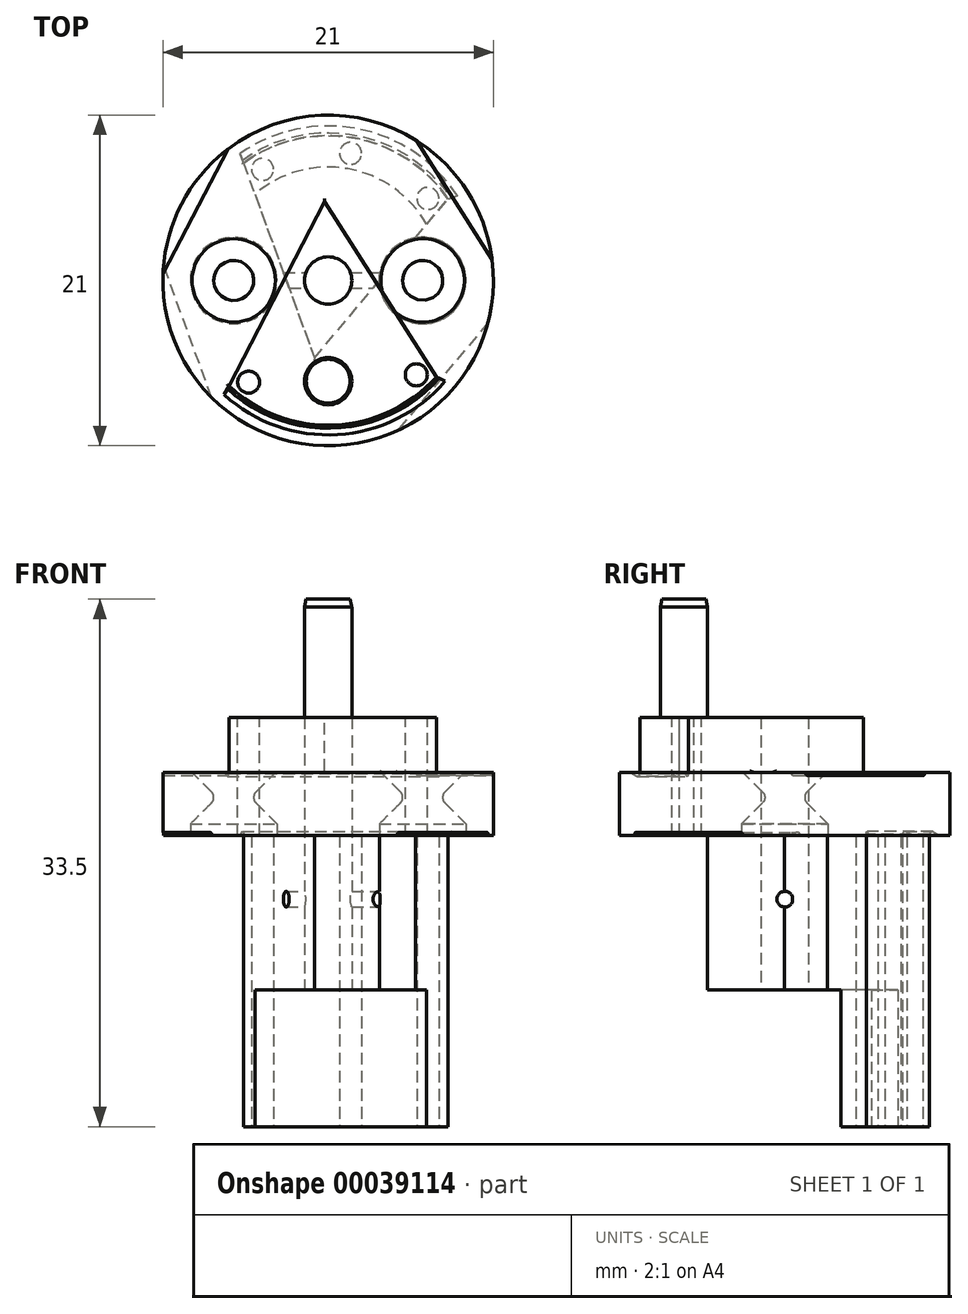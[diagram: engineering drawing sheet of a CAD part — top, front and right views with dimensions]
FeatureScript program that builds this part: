
annotation { "Feature Type Name" : "Feature", "Feature Type Description" : "" }
export const myFeature = defineFeature(function(context is Context, id is Id, definition is map)
    precondition{}
    {
        {
            var Q0;
            Q0=qCreatedBy(makeId("Front.planeOp"),FACE);
            var sketch = newSketch(context, id + "F0", { "sketchPlane" : qUnion([Q0])});
            skLineSegment(sketch, "E0.bottom", {"start": v(-9.2, 26) * mm, "end": v(0, 26) * mm});
            skLineSegment(sketch, "E0.top", {"start": v(-9.2, 0) * mm, "end": v(0, 0) * mm});
            skLineSegment(sketch, "E0.left", {"start": v(-9.2, 18.5) * mm, "end": v(-9.2, 0) * mm});
            skLineSegment(sketch, "E1.bottom", {"start": v(-9.2, 26) * mm, "end": v(-10.5, 26) * mm});
            skLineSegment(sketch, "E1.top", {"start": v(-9.2, 18.5) * mm, "end": v(-10.5, 18.5) * mm});
            skLineSegment(sketch, "E1.right", {"start": v(-10.5, 26) * mm, "end": v(-10.5, 18.5) * mm});
            skLineSegment(sketch, "E2", {"start": v(0, 0) * mm, "end": v(0, 26) * mm});
            skPoint(sketch, "E0.right.start.orphan", {"position": v(9.2, 26) * mm});
            skSolve(sketch);
        }
        {
            var Q0;
            Q0=makeQuery(id+"F0.imprint","IMPRINT",FACE,{"disambiguationData":[TD([[makeQuery(id+"F0.imprint","IMPRINT",EDGE,{"derivedFrom":sQuery(id+"F0.wireOp",EDGE,"E0.bottom")}),-1.0]])]});
            var Q1;
            Q1=sQuery(id+"F0.wireOp",EDGE,"E2");
            revolve(context, id + "F1", {"entities" : qUnion([Q0]), "axis" : qUnion([Q1]), "revolveType" : RevolveType.FULL});
        }
        {
            var Q0;
            Q0=makeQuery(id+"F1.opRevolve","SWEPT_FACE",FACE,{"disambiguationData":[OSD([sQuery(id+"F0.wireOp",EDGE,"E0.top")])]});
            var sketch = newSketch(context, id + "F2", { "sketchPlane" : qUnion([Q0])});
            skCircle(sketch, "E3", {"center": v(0, 0) * mm, "radius": 7.2 * mm});
            skSolve(sketch);
        }
        {
            var Q0;
            Q0=makeQuery(id+"F2.imprint","IMPRINT",FACE,{"disambiguationData":[TD([[makeQuery(id+"F2.imprint","IMPRINT",EDGE,{"derivedFrom":sQuery(id+"F2.wireOp",EDGE,"E3")}),1.0]])]});
            extrude(context, id + "F3", {"entities" : qUnion([Q0]), "operationType" : NewBodyOperationType.REMOVE, "oppositeDirection" : true, "depth" : 8.7 * mm});
        }
        {
            var Q0;
            Q0=makeQuery(id+"F3.boolean.opBoolean","COPY",FACE,{"derivedFrom":makeQuery(id+"F3.opExtrude","CAP_FACE",FACE,{"disambiguationData":[OSD([sQuery(id+"F2.wireOp",EDGE,"E3")])],"isStart":false})});
            var sketch = newSketch(context, id + "F4", { "sketchPlane" : qUnion([Q0])});
            skPoint(sketch, "E4", {"position": v(-5.84, -8.73) * mm});
            skLineSegment(sketch, "E5", {"start": v(-5.84, -8.73) * mm, "end": v(-0.87, 4.92) * mm});
            skLineSegment(sketch, "E6", {"start": v(-0.87, 4.92) * mm, "end": v(8.47, -6.2) * mm});
            skPoint(sketch, "E7", {"position": v(0, 3.89) * mm});
            skCircle(sketch, "E8", {"center": v(0, 0) * mm, "radius": 2.5 * mm, "construction": true});
            skCircle(sketch, "E9", {"center": v(0, 0) * mm, "radius": 1.5 * mm});
            skArc(sketch, "E10", {"start": v(8.47, -6.2) * mm, "mid": v(-1.82, 10.34) * mm, "end": v(-5.84, -8.73) * mm});
            skCircle(sketch, "E11", {"center": v(1.42, -8.08) * mm, "radius": 0.7 * mm});
            skCircle(sketch, "E12", {"center": v(6.33, -5.21) * mm, "radius": 0.7 * mm});
            skCircle(sketch, "E13", {"center": v(-4.17, -7.06) * mm, "radius": 0.7 * mm});
            skLineSegment(sketch, "E14", {"start": v(1.42, -8.08) * mm, "end": v(0, 0) * mm, "construction": true});
            skLineSegment(sketch, "E15", {"start": v(10.15, 2.68) * mm, "end": v(4.4, 9.53) * mm});
            skLineSegment(sketch, "E16", {"start": v(-7.4, 7.45) * mm, "end": v(-10.46, -0.95) * mm});
            skSolve(sketch);
        }
        {
            var Q0;
            Q0 = qSketchRegion(id + "F4", true);
            var Q1;
            Q1=makeQuery(id+"F1.opRevolve","SWEPT_FACE",FACE,{"disambiguationData":[OSD([sQuery(id+"F0.wireOp",EDGE,"E0.top")])]});
            extrude(context, id + "F5", {"entities" : qUnion([Q0]), "operationType" : NewBodyOperationType.REMOVE, "oppositeDirection" : true, "depth" : 9.8 * mm, "hasSecondDirection" : true, "secondDirectionBound" : SecondDirectionBoundingType.UP_TO_SURFACE, "secondDirectionOppositeDirection" : false, "secondDirectionBoundEntityFace" : qUnion([Q1]), "secondDirectionDepth" : 25 * mm});
        }
        {
            var Q0;
            {var subQ0=sQuery(id+"F4.wireOp",EDGE,"E15");Q0=makeQuery(id+"F4.imprint","IMPRINT",FACE,{"disambiguationData":[TD([[makeQuery(id+"F4.imprint","IMPRINT",EDGE,{"derivedFrom":subQ0}),-1.0]])]});}
            var Q1;
            {var subQ0=sQuery(id+"F4.wireOp",EDGE,"E16");Q1=makeQuery(id+"F4.imprint","IMPRINT",FACE,{"disambiguationData":[TD([[makeQuery(id+"F4.imprint","IMPRINT",EDGE,{"derivedFrom":subQ0}),-1.0]])]});}
            extrude(context, id + "F6", {"entities" : qUnion([Q0, Q1]), "operationType" : NewBodyOperationType.REMOVE, "oppositeDirection" : true, "depth" : 10 * mm});
        }
        {
            var Q0;
            Q0=makeQuery(id+"F1.opRevolve","SWEPT_FACE",FACE,{"disambiguationData":[OSD([sQuery(id+"F0.wireOp",EDGE,"E0.bottom"),sQuery(id+"F0.wireOp",EDGE,"E1.bottom")])]});
            var sketch = newSketch(context, id + "F7", { "sketchPlane" : qUnion([Q0])});
            skCircle(sketch, "E17", {"center": v(0, 0) * mm, "radius": 2.5 * mm, "construction": true});
            skLineSegment(sketch, "E18", {"start": v(7.59, -7.26) * mm, "end": v(-0.22, 5) * mm});
            skLineSegment(sketch, "E19", {"start": v(-0.22, 5) * mm, "end": v(-6.93, -7.9) * mm});
            skArc(sketch, "E20", {"start": v(7.59, -7.26) * mm, "mid": v(-0.46, 10.5) * mm, "end": v(-6.93, -7.9) * mm});
            skLineSegment(sketch, "E21", {"start": v(10.42, 1.33) * mm, "end": v(5.6, 8.88) * mm});
            skLineSegment(sketch, "E22", {"start": v(-10.5, 0.42) * mm, "end": v(-6.36, 8.35) * mm});
            skArc(sketch, "E23", {"start": v(-6.3, -6.7) * mm, "mid": v(0.4, -9.2) * mm, "end": v(6.87, -6.12) * mm});
            skArc(sketch, "E24", {"start": v(-6.93, -7.9) * mm, "mid": v(0.46, -10.5) * mm, "end": v(7.59, -7.26) * mm});
            skSolve(sketch);
        }
        {
            var Q0;
            {var subQ0=sQuery(id+"F7.wireOp",EDGE,"E21");Q0=makeQuery(id+"F7.imprint","IMPRINT",FACE,{"disambiguationData":[TD([[makeQuery(id+"F7.imprint","IMPRINT",EDGE,{"derivedFrom":subQ0}),-1.0]])]});}
            var Q1;
            {var subQ5=sQuery(id+"F7.wireOp",EDGE,"E18");Q1=makeQuery(id+"F7.imprint","IMPRINT",FACE,{"disambiguationData":[TD([[makeQuery(id+"F7.imprint","IMPRINT",EDGE,{"derivedFrom":subQ5}),-1.0]])]});}
            var Q2;
            {var subQ0=sQuery(id+"F7.wireOp",EDGE,"E22");Q2=makeQuery(id+"F7.imprint","IMPRINT",FACE,{"disambiguationData":[TD([[makeQuery(id+"F7.imprint","IMPRINT",EDGE,{"derivedFrom":subQ0}),1.0]])]});}
            var Q3;
            Q3=makeQuery(id+"F7.imprint","IMPRINT",FACE,{"disambiguationData":[TD([[makeQuery(id+"F7.imprint","IMPRINT",EDGE,{"derivedFrom":sQuery(id+"F7.wireOp",EDGE,"75845bfa-6e58-4d6f-9768-84c6fc873f1d")}),1.0]])]});
            var Q4;
            Q4=makeQuery(id+"F7.imprint","IMPRINT",FACE,{"disambiguationData":[TD([[makeQuery(id+"F7.imprint","IMPRINT",EDGE,{"derivedFrom":sQuery(id+"F7.wireOp",EDGE,"bd788875-77d4-44b3-9050-4ba9302ed74b")}),1.0]])]});
            var Q5;
            {var subQ1=sQuery(id+"F7.wireOp",EDGE,"E23");Q5=makeQuery(id+"F7.imprint","IMPRINT",FACE,{"disambiguationData":[TD([[makeQuery(id+"F7.imprint","IMPRINT",EDGE,{"derivedFrom":subQ1}),-1.0]])]});}
            extrude(context, id + "F8", {"entities" : qUnion([Q0, Q1, Q2, Q3, Q4, Q5]), "operationType" : NewBodyOperationType.REMOVE, "oppositeDirection" : true, "depth" : 3.5 * mm});
        }
        {
            var Q0;
            Q0=makeQuery(id+"F1.opRevolve","SWEPT_FACE",FACE,{"disambiguationData":[OSD([sQuery(id+"F0.wireOp",EDGE,"E0.bottom"),sQuery(id+"F0.wireOp",EDGE,"E1.bottom")])]});
            var sketch = newSketch(context, id + "F9", { "sketchPlane" : qUnion([Q0])});
            skCircle(sketch, "E25", {"center": v(0, 0) * mm, "radius": 1.5 * mm});
            skCircle(sketch, "E26", {"center": v(0, -6.4) * mm, "radius": 1.5 * mm});
            skCircle(sketch, "E27", {"center": v(5.6, -6) * mm, "radius": 0.7 * mm});
            skCircle(sketch, "E28", {"center": v(-5.05, -6.46) * mm, "radius": 0.7 * mm});
            skSolve(sketch);
        }
        {
            var Q0;
            Q0=makeQuery(id+"F9.imprint","IMPRINT",FACE,{"disambiguationData":[TD([[makeQuery(id+"F9.imprint","IMPRINT",EDGE,{"derivedFrom":sQuery(id+"F9.wireOp",EDGE,"E25")}),1.0]])]});
            var Q1;
            Q1=makeQuery(id+"F9.imprint","IMPRINT",FACE,{"disambiguationData":[TD([[makeQuery(id+"F9.imprint","IMPRINT",EDGE,{"derivedFrom":sQuery(id+"F9.wireOp",EDGE,"E27")}),1.0]])]});
            var Q2;
            Q2=makeQuery(id+"F9.imprint","IMPRINT",FACE,{"disambiguationData":[TD([[makeQuery(id+"F9.imprint","IMPRINT",EDGE,{"derivedFrom":sQuery(id+"F9.wireOp",EDGE,"E28")}),1.0]])]});
            extrude(context, id + "F10", {"entities" : qUnion([Q0, Q1, Q2]), "operationType" : NewBodyOperationType.REMOVE, "endBound" : BoundingType.UP_TO_NEXT, "oppositeDirection" : true, "depth" : 25 * mm});
        }
        {
            var Q0;
            {var subQ0=sQuery(id+"F7.wireOp",EDGE,"E21");Q0=makeQuery(id+"F7.imprint","IMPRINT",FACE,{"disambiguationData":[TD([[makeQuery(id+"F7.imprint","IMPRINT",EDGE,{"derivedFrom":subQ0}),-1.0]])]});}
            var Q1;
            {var subQ0=sQuery(id+"F7.wireOp",EDGE,"E22");Q1=makeQuery(id+"F7.imprint","IMPRINT",FACE,{"disambiguationData":[TD([[makeQuery(id+"F7.imprint","IMPRINT",EDGE,{"derivedFrom":subQ0}),1.0]])]});}
            extrude(context, id + "F11", {"entities" : qUnion([Q0, Q1]), "operationType" : NewBodyOperationType.REMOVE, "oppositeDirection" : true, "depth" : 3.7 * mm});
        }
        {
            var Q0;
            Q0=makeQuery(id+"F9.imprint","IMPRINT",FACE,{"disambiguationData":[TD([[makeQuery(id+"F9.imprint","IMPRINT",EDGE,{"derivedFrom":sQuery(id+"F9.wireOp",EDGE,"E26")}),1.0]])]});
            extrude(context, id + "F12", {"entities" : qUnion([Q0]), "operationType" : NewBodyOperationType.ADD, "depth" : 7.5 * mm});
        }
        {
            var Q0;
            Q0=makeQuery(id+"F12.opExtrude","CAP_EDGE",EDGE,{"disambiguationData":[OSD([sQuery(id+"F9.wireOp",EDGE,"E26")])],"isStart":false});
            chamfer(context, id + "F13", {"entities" : qUnion([Q0]), "chamferType" : ChamferType.OFFSET_ANGLE, "width" : 0.5 * mm, "oppositeDirection" : true, "angle" : 12 * degree, "tangentPropagation" : true});
        }
        {
            var Q0;
            Q0=qCreatedBy(makeId("Front.planeOp"),FACE);
            var sketch = newSketch(context, id + "F14", { "sketchPlane" : qUnion([Q0])});
            skLineSegment(sketch, "E29", {"start": v(-6, 22.5) * mm, "end": v(-6, 19.26) * mm});
            skLineSegment(sketch, "E30", {"start": v(-6, 22.5) * mm, "end": v(-8.65, 22.5) * mm});
            skLineSegment(sketch, "E31", {"start": v(-8.65, 22.5) * mm, "end": v(-7.42, 21.27) * mm});
            skLineSegment(sketch, "E32", {"start": v(-8.75, 19.23) * mm, "end": v(-7.42, 20.56) * mm});
            skArc(sketch, "E33", {"start": v(-7.42, 20.56) * mm, "mid": v(-7.27, 20.91) * mm, "end": v(-7.42, 21.27) * mm});
            skCircle(sketch, "E34", {"center": v(-6, 18.5) * mm, "radius": 2.5 * mm, "construction": true});
            skLineSegment(sketch, "E35.top", {"start": v(-6, 18.5) * mm, "end": v(-8.75, 18.5) * mm});
            skLineSegment(sketch, "E35.left", {"start": v(-6, 19.26) * mm, "end": v(-6, 18.5) * mm});
            skLineSegment(sketch, "E35.right", {"start": v(-8.75, 19.23) * mm, "end": v(-8.75, 18.5) * mm});
            skSolve(sketch);
        }
        {
            var Q0;
            Q0 = qSketchRegion(id + "F14", true);
            var Q1;
            Q1=sQuery(id+"F14.wireOp",EDGE,"E29");
            revolve(context, id + "F15", {"operationType" : NewBodyOperationType.REMOVE, "entities" : qUnion([Q0]), "axis" : qUnion([Q1]), "revolveType" : RevolveType.FULL, "oppositeDirection" : true});
        }
        {
            var Q0;
            Q0=qCreatedBy(makeId("Front.planeOp"),FACE);
            var sketch = newSketch(context, id + "F16", { "sketchPlane" : qUnion([Q0])});
            skLineSegment(sketch, "E36", {"start": v(6, 22.5) * mm, "end": v(6, 21.29) * mm});
            skLineSegment(sketch, "E37", {"start": v(6, 22.5) * mm, "end": v(3.35, 22.5) * mm});
            skLineSegment(sketch, "E38", {"start": v(3.35, 22.5) * mm, "end": v(4.58, 21.27) * mm});
            skLineSegment(sketch, "E39", {"start": v(3.25, 19.23) * mm, "end": v(4.58, 20.56) * mm});
            skArc(sketch, "E40", {"start": v(4.58, 20.56) * mm, "mid": v(4.73, 20.91) * mm, "end": v(4.58, 21.27) * mm});
            skCircle(sketch, "E41", {"center": v(6, 18.5) * mm, "radius": 2.5 * mm, "construction": true});
            skLineSegment(sketch, "E42.top", {"start": v(6, 18.5) * mm, "end": v(3.25, 18.5) * mm});
            skLineSegment(sketch, "E42.left", {"start": v(6, 21.29) * mm, "end": v(6, 18.5) * mm});
            skLineSegment(sketch, "E42.right", {"start": v(3.25, 19.23) * mm, "end": v(3.25, 18.5) * mm});
            skLineSegment(sketch, "E43", {"start": v(3.25, 18.5) * mm, "end": v(3.25, 8.7) * mm});
            skLineSegment(sketch, "E44", {"start": v(3.25, 8.7) * mm, "end": v(6, 8.7) * mm});
            skLineSegment(sketch, "E45", {"start": v(6, 8.7) * mm, "end": v(6, 18.5) * mm});
            skSolve(sketch);
        }
        {
            var Q0;
            Q0=makeQuery(id+"F16.imprint","IMPRINT",FACE,{"disambiguationData":[TD([[makeQuery(id+"F16.imprint","IMPRINT",EDGE,{"derivedFrom":sQuery(id+"F16.wireOp",EDGE,"E36")}),-1.0]])]});
            var Q1;
            Q1=makeQuery(id+"F16.imprint","IMPRINT",FACE,{"disambiguationData":[TD([[makeQuery(id+"F16.imprint","IMPRINT",EDGE,{"derivedFrom":sQuery(id+"F16.wireOp",EDGE,"E42.top")}),1.0]])]});
            var Q2;
            Q2=sQuery(id+"F16.wireOp",EDGE,"E42.left");
            revolve(context, id + "F17", {"operationType" : NewBodyOperationType.REMOVE, "entities" : qUnion([Q0, Q1]), "axis" : qUnion([Q2]), "revolveType" : RevolveType.FULL, "oppositeDirection" : true});
        }
        {
            var Q0;
            Q0=makeQuery(id+"F8.boolean.opBoolean","COPY",FACE,{"derivedFrom":makeQuery(id+"F8.opExtrude","SWEPT_FACE",FACE,{"disambiguationData":[OSD([sQuery(id+"F7.wireOp",EDGE,"E19")])]})});
            var sketch = newSketch(context, id + "F18", { "sketchPlane" : qUnion([Q0])});
            skLineSegment(sketch, "E46", {"start": v(8.85, 22.5) * mm, "end": v(9.49, 22.5) * mm});
            skLineSegment(sketch, "E47", {"start": v(9.49, 22.5) * mm, "end": v(9.05, 22.25) * mm});
            skPoint(sketch, "E48", {"position": v(9.05, 22.45) * mm});
            skArc(sketch, "E49", {"start": v(9.05, 22.25) * mm, "mid": v(8.91, 22.3) * mm, "end": v(8.85, 22.45) * mm});
            skLineSegment(sketch, "E50", {"start": v(8.85, 22.5) * mm, "end": v(8.85, 22.45) * mm});
            skSolve(sketch);
        }
        {
            var Q0;
            Q0 = qSketchRegion(id + "F18", true);
            var Q1;
            Q1=makeQuery(id+"F8.boolean.opBoolean","COPY",EDGE,{"derivedFrom":makeQuery(id+"F8.opExtrude","CAP_EDGE",EDGE,{"disambiguationData":[OSD([sQuery(id+"F7.wireOp",EDGE,"E23")])],"isStart":false})});
            sweep(context, id + "F19", {"operationType" : NewBodyOperationType.REMOVE, "profiles" : qUnion([Q0]), "path" : qUnion([Q1])});
        }
        {
            var Q0;
            Q0=makeQuery(id+"F5.boolean.opBoolean","COPY",FACE,{"derivedFrom":makeQuery(id+"F5.opExtrude","SWEPT_FACE",FACE,{"disambiguationData":[OSD([sQuery(id+"F4.wireOp",EDGE,"E5")])]})});
            var sketch = newSketch(context, id + "F20", { "sketchPlane" : qUnion([Q0])});
            skLineSegment(sketch, "E51", {"start": v(-8.85, 18.5) * mm, "end": v(-9.49, 18.5) * mm});
            skLineSegment(sketch, "E52", {"start": v(-9.49, 18.5) * mm, "end": v(-9.05, 18.75) * mm});
            skPoint(sketch, "E53", {"position": v(-9.05, 18.55) * mm});
            skArc(sketch, "E54", {"start": v(-9.05, 18.75) * mm, "mid": v(-8.91, 18.7) * mm, "end": v(-8.85, 18.55) * mm});
            skLineSegment(sketch, "E55", {"start": v(-8.85, 18.55) * mm, "end": v(-8.85, 18.5) * mm});
            skSolve(sketch);
        }
        {
            var Q0;
            Q0=makeQuery(id+"F20.imprint","IMPRINT",FACE,{"disambiguationData":[TD([[makeQuery(id+"F20.imprint","IMPRINT",EDGE,{"derivedFrom":sQuery(id+"F20.wireOp",EDGE,"E51")}),-1.0]])]});
            var Q1;
            Q1=makeQuery(id+"F1.opRevolve","SWEPT_EDGE",EDGE,{"disambiguationData":[OSD([sQuery(id+"F0.wireOp",EDGE,"E0.left"),sQuery(id+"F0.wireOp",EDGE,"E1.top")])]});
            sweep(context, id + "F21", {"operationType" : NewBodyOperationType.REMOVE, "profiles" : qUnion([Q0]), "path" : qUnion([Q1])});
        }
        {
            var Q0;
            Q0=makeQuery(id+"F5.boolean.opBoolean","COPY",EDGE,{"derivedFrom":makeQuery(id+"F5.opExtrude","CAP_EDGE",EDGE,{"disambiguationData":[OSD([sQuery(id+"F4.wireOp",EDGE,"E5")])],"isStart":false})});
            fillet(context, id + "F22", {"entities" : qUnion([Q0]), "radius" : 0.1 * mm, "tangentPropagation" : true, "allowEdgeOverflow" : false});
        }
        {
            var Q0;
            {var subQ0=sQuery(id+"F4.wireOp",EDGE,"E6");var subQ1=sQuery(id+"F4.wireOp",EDGE,"E5");Q0=makeQuery(id+"F17.boolean.opBoolean","SPLIT",EDGE,{"disambiguationData":[TD([makeQuery(id+"F5.boolean.opBoolean","COPY",FACE,{"derivedFrom":makeQuery(id+"F5.opExtrude","SWEPT_FACE",FACE,{"disambiguationData":[OSD([subQ1])]})})])],"derivedFrom":makeQuery(id+"F5.boolean.opBoolean","COPY",EDGE,{"derivedFrom":makeQuery(id+"F5.opExtrude","CAP_EDGE",EDGE,{"disambiguationData":[OSD([subQ0])],"isStart":false})})});}
            var Q1;
            {var subQ0=sQuery(id+"F4.wireOp",EDGE,"E6");Q1=makeQuery(id+"F17.boolean.opBoolean","SPLIT",EDGE,{"disambiguationData":[TD([makeQuery(id+"F1.opRevolve","SWEPT_FACE",FACE,{"disambiguationData":[OSD([sQuery(id+"F0.wireOp",EDGE,"E0.left")])]})])],"derivedFrom":makeQuery(id+"F5.boolean.opBoolean","COPY",EDGE,{"derivedFrom":makeQuery(id+"F5.opExtrude","CAP_EDGE",EDGE,{"disambiguationData":[OSD([subQ0])],"isStart":false})})});}
            fillet(context, id + "F23", {"entities" : qUnion([Q0, Q1]), "radius" : 0.1 * mm, "tangentPropagation" : true, "allowEdgeOverflow" : false});
        }
        {
            var Q0;
            Q0=makeQuery(id+"F8.boolean.opBoolean","COPY",EDGE,{"derivedFrom":makeQuery(id+"F8.opExtrude","CAP_EDGE",EDGE,{"disambiguationData":[OSD([sQuery(id+"F7.wireOp",EDGE,"E18")])],"isStart":false})});
            var Q1;
            Q1=makeQuery(id+"F8.boolean.opBoolean","COPY",EDGE,{"derivedFrom":makeQuery(id+"F8.opExtrude","CAP_EDGE",EDGE,{"disambiguationData":[OSD([sQuery(id+"F7.wireOp",EDGE,"E19")])],"isStart":false})});
            fillet(context, id + "F24", {"entities" : qUnion([Q0, Q1]), "radius" : 0.1 * mm, "tangentPropagation" : true, "allowEdgeOverflow" : false});
        }
        {
            var Q0;
            Q0=makeQuery(id+"F11.boolean.opBoolean","COPY",EDGE,{"derivedFrom":makeQuery(id+"F11.opExtrude","CAP_EDGE",EDGE,{"disambiguationData":[OSD([sQuery(id+"F7.wireOp",EDGE,"E21")])],"isStart":false})});
            var Q1;
            Q1=makeQuery(id+"F11.boolean.opBoolean","COPY",EDGE,{"derivedFrom":makeQuery(id+"F11.opExtrude","CAP_EDGE",EDGE,{"disambiguationData":[OSD([sQuery(id+"F7.wireOp",EDGE,"E22")])],"isStart":false})});
            fillet(context, id + "F25", {"entities" : qUnion([Q0, Q1]), "radius" : 0.1 * mm, "tangentPropagation" : true, "allowEdgeOverflow" : false});
        }
        {
            var Q0;
            Q0=makeQuery(id+"F6.boolean.opBoolean","COPY",EDGE,{"derivedFrom":makeQuery(id+"F6.opExtrude","CAP_EDGE",EDGE,{"disambiguationData":[OSD([sQuery(id+"F4.wireOp",EDGE,"E15")])],"isStart":false})});
            var Q1;
            Q1=makeQuery(id+"F6.boolean.opBoolean","COPY",EDGE,{"derivedFrom":makeQuery(id+"F6.opExtrude","CAP_EDGE",EDGE,{"disambiguationData":[OSD([sQuery(id+"F4.wireOp",EDGE,"E16")])],"isStart":false})});
            fillet(context, id + "F26", {"entities" : qUnion([Q0, Q1]), "radius" : 0.1 * mm, "tangentPropagation" : true, "allowEdgeOverflow" : false});
        }
        {
            var Q0;
            Q0=makeQuery(id+"F8.boolean.opBoolean","COPY",FACE,{"derivedFrom":makeQuery(id+"F8.opExtrude","CAP_FACE",FACE,{"disambiguationData":[OSD([sQuery(id+"F7.wireOp",EDGE,"E18"),sQuery(id+"F7.wireOp",EDGE,"E19"),sQuery(id+"F7.wireOp",EDGE,"E20"),sQuery(id+"F7.wireOp",EDGE,"E23"),sQuery(id+"F7.wireOp",EDGE,"E24")])],"isStart":false})});
            var sketch = newSketch(context, id + "F27", { "sketchPlane" : qUnion([Q0])});
            skArc(sketch, "E56", {"start": v(6.4, -8.83) * mm, "mid": v(-2.5, -10.6) * mm, "end": v(-9.67, -5.03) * mm});
            skArc(sketch, "E57", {"start": v(-5, -7.84) * mm, "mid": v(0, -9.3) * mm, "end": v(5, -7.84) * mm});
            skArc(sketch, "E58", {"start": v(6.6, -6.42) * mm, "mid": v(5.83, -7.12) * mm, "end": v(5, -7.72) * mm});
            skLineSegment(sketch, "E59", {"start": v(9.67, -5.03) * mm, "end": v(0, 0) * mm, "construction": true});
            skLineSegment(sketch, "E60", {"start": v(-9.67, -5.03) * mm, "end": v(0, 0) * mm, "construction": true});
            skLineSegment(sketch, "E61", {"start": v(5, -7.84) * mm, "end": v(5, -7.72) * mm});
            skLineSegment(sketch, "E62", {"start": v(-5, -7.84) * mm, "end": v(-5, -7.72) * mm});
            skArc(sketch, "E63.trimOffspring", {"start": v(-5, -7.72) * mm, "mid": v(-5.83, -7.12) * mm, "end": v(-6.6, -6.42) * mm});
            skArc(sketch, "E64", {"start": v(-6, -3.99) * mm, "mid": v(1, -7.13) * mm, "end": v(6.86, -2.18) * mm, "construction": true});
            skLineSegment(sketch, "E65", {"start": v(-6.6, -6.42) * mm, "end": v(-5.54, -4.6) * mm});
            skLineSegment(sketch, "E66", {"start": v(6.6, -6.42) * mm, "end": v(5.54, -4.6) * mm});
            skArc(sketch, "E67", {"start": v(-5.54, -4.6) * mm, "mid": v(-5.68, -4.43) * mm, "end": v(-5.81, -4.25) * mm});
            skLineSegment(sketch, "E68", {"start": v(-5.81, -4.25) * mm, "end": v(-8.16, -4.25) * mm});
            skLineSegment(sketch, "E69", {"start": v(-8.16, -4.25) * mm, "end": v(-9.67, -5.03) * mm});
            skArc(sketch, "E70", {"start": v(5.54, -4.6) * mm, "mid": v(5.68, -4.43) * mm, "end": v(5.81, -4.25) * mm});
            skLineSegment(sketch, "E71", {"start": v(5.81, -4.25) * mm, "end": v(8.16, -4.25) * mm});
            skLineSegment(sketch, "E72", {"start": v(8.16, -4.25) * mm, "end": v(8.74, -4.55) * mm});
            skPoint(sketch, "E73.visualSharp", {"position": v(9.67, -5.03) * mm});
            skArc(sketch, "E73.filletArc", {"start": v(9.11, -5.98) * mm, "mid": v(9.24, -5.18) * mm, "end": v(8.74, -4.55) * mm});
            skPoint(sketch, "E74.visualSharp", {"position": v(-9.67, -5.03) * mm});
            skLineSegment(sketch, "E75", {"start": v(5.26, -10.1) * mm, "end": v(5.59, -10.73) * mm});
            skLineSegment(sketch, "E76", {"start": v(5.59, -10.73) * mm, "end": v(5.76, -10.64) * mm});
            skLineSegment(sketch, "E77", {"start": v(5.76, -10.64) * mm, "end": v(6.4, -8.83) * mm});
            skLineSegment(sketch, "E78", {"start": v(6.4, -8.83) * mm, "end": v(7.12, -9.83) * mm, "construction": true});
            skPoint(sketch, "E79.newPointA", {"position": v(5.03, -9.67) * mm});
            skArc(sketch, "E79.filletArc", {"start": v(5.26, -10.1) * mm, "mid": v(4.98, -9.86) * mm, "end": v(4.6, -9.88) * mm});
            skArc(sketch, "E80", {"start": v(9.11, -5.98) * mm, "mid": v(7.88, -7.53) * mm, "end": v(6.4, -8.83) * mm});
            skSolve(sketch);
        }
        {
            var Q0;
            Q0 = qSketchRegion(id + "F27", true);
            extrude(context, id + "F28", {"entities" : qUnion([Q0]), "depth" : 0.5 * mm});
        }
        {
            var Q0;
            Q0=makeQuery(id+"F28.opExtrude","SWEPT_BODY",BODY,{"disambiguationData":[OSD([sQuery(id+"F27.wireOp",EDGE,"E56"),sQuery(id+"F27.wireOp",EDGE,"E57"),sQuery(id+"F27.wireOp",EDGE,"E58"),sQuery(id+"F27.wireOp",EDGE,"E61"),sQuery(id+"F27.wireOp",EDGE,"E62"),sQuery(id+"F27.wireOp",EDGE,"E63.trimOffspring"),sQuery(id+"F27.wireOp",EDGE,"E65"),sQuery(id+"F27.wireOp",EDGE,"E66"),sQuery(id+"F27.wireOp",EDGE,"E67"),sQuery(id+"F27.wireOp",EDGE,"E68"),sQuery(id+"F27.wireOp",EDGE,"E69"),sQuery(id+"F27.wireOp",EDGE,"E70"),sQuery(id+"F27.wireOp",EDGE,"E71"),sQuery(id+"F27.wireOp",EDGE,"E72"),sQuery(id+"F27.wireOp",EDGE,"E73.filletArc"),sQuery(id+"F27.wireOp",EDGE,"E75"),sQuery(id+"F27.wireOp",EDGE,"E76"),sQuery(id+"F27.wireOp",EDGE,"E77"),sQuery(id+"F27.wireOp",EDGE,"E79.filletArc"),sQuery(id+"F27.wireOp",EDGE,"E80")])]});
            transform(context, id + "F29", {"entities" : qUnion([Q0]), "transformType" : TransformType.TRANSLATION_3D, "dx" : 0 * mm, "dy" : 0 * mm, "dz" : 0.5 * mm, "makeCopy" : true});
        }
        {
            var Q0;
            Q0=makeQuery(id+"F29.opPattern","COPY",BODY,{"derivedFrom":makeQuery(id+"F28.opExtrude","SWEPT_BODY",BODY,{"disambiguationData":[OSD([sQuery(id+"F27.wireOp",EDGE,"E56"),sQuery(id+"F27.wireOp",EDGE,"E57"),sQuery(id+"F27.wireOp",EDGE,"E58"),sQuery(id+"F27.wireOp",EDGE,"E61"),sQuery(id+"F27.wireOp",EDGE,"E62"),sQuery(id+"F27.wireOp",EDGE,"E63.trimOffspring"),sQuery(id+"F27.wireOp",EDGE,"E65"),sQuery(id+"F27.wireOp",EDGE,"E66"),sQuery(id+"F27.wireOp",EDGE,"E67"),sQuery(id+"F27.wireOp",EDGE,"E68"),sQuery(id+"F27.wireOp",EDGE,"E69"),sQuery(id+"F27.wireOp",EDGE,"E70"),sQuery(id+"F27.wireOp",EDGE,"E71"),sQuery(id+"F27.wireOp",EDGE,"E72"),sQuery(id+"F27.wireOp",EDGE,"E73.filletArc"),sQuery(id+"F27.wireOp",EDGE,"E75"),sQuery(id+"F27.wireOp",EDGE,"E76"),sQuery(id+"F27.wireOp",EDGE,"E77"),sQuery(id+"F27.wireOp",EDGE,"E79.filletArc"),sQuery(id+"F27.wireOp",EDGE,"E80")])]}),"instanceName":"1"});
            deleteBodies(context, id + "F30", {"entities" : qUnion([Q0])});
        }
        {
            var Q0;
            Q0=makeQuery(id+"F28.opExtrude","SWEPT_BODY",BODY,{"disambiguationData":[OSD([sQuery(id+"F27.wireOp",EDGE,"E56"),sQuery(id+"F27.wireOp",EDGE,"E57"),sQuery(id+"F27.wireOp",EDGE,"E58"),sQuery(id+"F27.wireOp",EDGE,"E61"),sQuery(id+"F27.wireOp",EDGE,"E62"),sQuery(id+"F27.wireOp",EDGE,"E63.trimOffspring"),sQuery(id+"F27.wireOp",EDGE,"E65"),sQuery(id+"F27.wireOp",EDGE,"E66"),sQuery(id+"F27.wireOp",EDGE,"E67"),sQuery(id+"F27.wireOp",EDGE,"E68"),sQuery(id+"F27.wireOp",EDGE,"E69"),sQuery(id+"F27.wireOp",EDGE,"E70"),sQuery(id+"F27.wireOp",EDGE,"E71"),sQuery(id+"F27.wireOp",EDGE,"E72"),sQuery(id+"F27.wireOp",EDGE,"E73.filletArc"),sQuery(id+"F27.wireOp",EDGE,"E75"),sQuery(id+"F27.wireOp",EDGE,"E76"),sQuery(id+"F27.wireOp",EDGE,"E77"),sQuery(id+"F27.wireOp",EDGE,"E79.filletArc"),sQuery(id+"F27.wireOp",EDGE,"E80")])]});
            deleteBodies(context, id + "F31", {"entities" : qUnion([Q0])});
        }
        {
            var Q0;
            Q0=qCreatedBy(makeId("Right.planeOp"),FACE);
            var sketch = newSketch(context, id + "F32", { "sketchPlane" : qUnion([Q0])});
            skCircle(sketch, "E81", {"center": v(0, 14.45) * mm, "radius": 0.5 * mm});
            skSolve(sketch);
        }
        {
            var Q0;
            Q0=makeQuery(id+"F32.imprint","IMPRINT",FACE,{"disambiguationData":[TD([[makeQuery(id+"F32.imprint","IMPRINT",EDGE,{"derivedFrom":sQuery(id+"F32.wireOp",EDGE,"E81")}),1.0]])]});
            var Q1;
            Q1=makeQuery(id+"F5.boolean.opBoolean","COPY",FACE,{"derivedFrom":makeQuery(id+"F5.opExtrude","SWEPT_FACE",FACE,{"disambiguationData":[OSD([sQuery(id+"F4.wireOp",EDGE,"E5")])]})});
            var Q2;
            {var subQ0=sQuery(id+"F4.wireOp",EDGE,"E5");var subQ1=sQuery(id+"F4.wireOp",EDGE,"E6");Q2=makeQuery(id+"F17.boolean.opBoolean","SPLIT",FACE,{"disambiguationData":[TD([makeQuery(id+"F5.boolean.opBoolean","COPY",FACE,{"derivedFrom":makeQuery(id+"F5.opExtrude","SWEPT_FACE",FACE,{"disambiguationData":[OSD([subQ0])]})})])],"derivedFrom":makeQuery(id+"F5.boolean.opBoolean","COPY",FACE,{"derivedFrom":makeQuery(id+"F5.opExtrude","SWEPT_FACE",FACE,{"disambiguationData":[OSD([subQ1])]})})});}
            extrude(context, id + "F33", {"entities" : qUnion([Q0]), "operationType" : NewBodyOperationType.REMOVE, "endBound" : BoundingType.UP_TO_SURFACE, "oppositeDirection" : true, "endBoundEntityFace" : qUnion([Q1]), "depth" : 25 * mm, "hasSecondDirection" : true, "secondDirectionBound" : SecondDirectionBoundingType.UP_TO_SURFACE, "secondDirectionOppositeDirection" : false, "secondDirectionBoundEntityFace" : qUnion([Q2]), "secondDirectionDepth" : 25 * mm});
        }
    });
